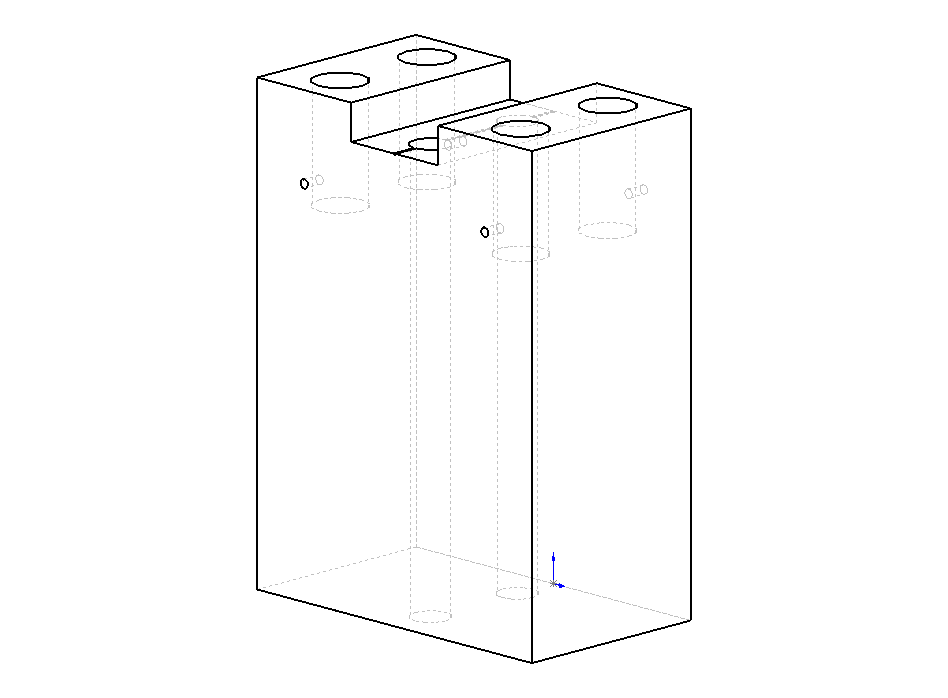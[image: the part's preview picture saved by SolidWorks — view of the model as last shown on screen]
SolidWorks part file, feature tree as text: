
SOLIDWORKS PART (.sldprt)
format: sldprt  version: not decoded by parser v0  size: 559,104 bytes
history: native  units: mm
features: sketch x7, cut_extrude x4, material x1, extrude x1, hole x1, mirror x1 + 1 further entry (+11 scaffold rows collapsed)
feature tree (27):
  scaffold x11  (default folders/planes/origin — collapsed)
  material  "Material <not specified>"
  "Origin"  ID=-1
  sketch  "Sketch1"  dims[D1=52.0mm D2=38.0mm]
  extrude  "Extrude1"  Depth=22mm
  sketch  "Sketch2"  dims[c1.D1=~4.331845mm c1.D2=~4.331845mm c1.D3=5.85mm c2.D1=25.0mm c2.D2=12.0mm]
  cut_extrude  "Cut-Extrude1"  Depth=12.7mm
  sketch  "Sketch5"  dims[D1=12.0mm]
  cut_extrude  "Cut-Extrude4"  Depth=4mm
  hole  "#8 Clearance Hole1"  Diameter=4.3053mm Depth=48mm
  sketch  "Sketch7"  dims[D1=12.0mm]
  sketch  "Sketch6"  dims[hole-wizard template sketch: 60 standard entries collapsed; hole parameters kept: c18.Thru Hole Depth=48.0mm]
  sketch  "Sketch8"  dims[D1=1.016mm D2=9.525mm]
  cut_extrude  "Cut-Extrude5"  [1 undecoded]
  mirror  "Mirror1"
  sketch  "Sketch9"  dims[D1=0.25mm]
  cut_extrude  "Cut-Extrude6"  Depth=0.1mm
decode coverage: 12 of 14 modeling features carry decoded parameters; 1 rows unclassified (native names shown)
note: ~ marks probable driven/reference dimensions
note: 1 parameter value undecoded
note: suppression state not decoded; provenance and decode notes live in map.json
